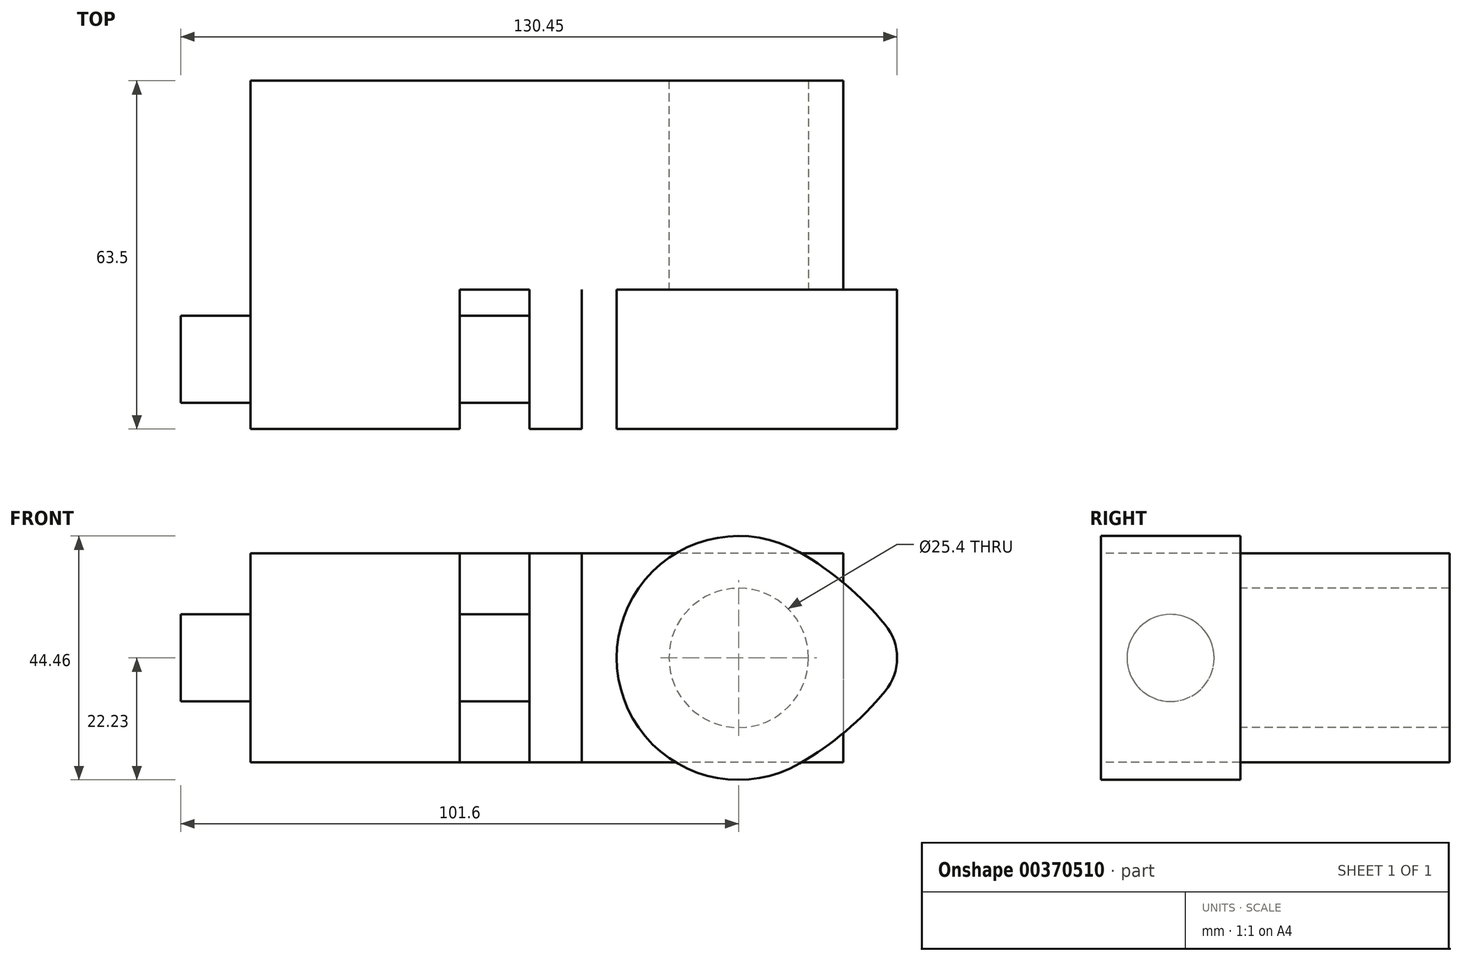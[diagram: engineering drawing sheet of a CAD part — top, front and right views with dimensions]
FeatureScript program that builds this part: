
annotation { "Feature Type Name" : "Feature", "Feature Type Description" : "" }
export const myFeature = defineFeature(function(context is Context, id is Id, definition is map)
    precondition{}
    {
        {
            var Q0;
            Q0=qCreatedBy(makeId("Front.planeOp"),FACE);
            var sketch = newSketch(context, id + "F0", { "sketchPlane" : qUnion([Q0])});
            skArc(sketch, "E0", {"start": v(11.11, 19.25) * mm, "mid": v(-22.22, 0) * mm, "end": v(11.11, -19.25) * mm});
            skLineSegment(sketch, "E1", {"start": v(0, 0) * mm, "end": v(-21.9, 37.92) * mm, "construction": true});
            skArc(sketch, "E2", {"start": v(11.11, -19.25) * mm, "mid": v(19.5, -13.35) * mm, "end": v(26.68, -6.05) * mm});
            skLineSegment(sketch, "E3", {"start": v(0, 0) * mm, "end": v(-17.46, -30.25) * mm, "construction": true});
            skArc(sketch, "E4", {"start": v(26.68, 6.05) * mm, "mid": v(19.5, 13.35) * mm, "end": v(11.11, 19.25) * mm});
            skCircle(sketch, "E5", {"center": v(0, 0) * mm, "radius": 12.7 * mm});
            skPoint(sketch, "E6.visualSharp", {"position": v(31.03, 0) * mm});
            skArc(sketch, "E6.filletArc", {"start": v(26.68, -6.05) * mm, "mid": v(28.85, 0) * mm, "end": v(26.68, 6.05) * mm});
            skSolve(sketch);
        }
        {
            var Q0;
            Q0=makeQuery(id+"F0.imprint","IMPRINT",FACE,{"disambiguationData":[TD([[makeQuery(id+"F0.imprint","IMPRINT",EDGE,{"derivedFrom":sQuery(id+"F0.wireOp",EDGE,"E0")}),1.0]])]});
            extrude(context, id + "F1", {"entities" : qUnion([Q0]), "depth" : 25.4 * mm});
        }
        {
            var Q0;
            Q0=qCreatedBy(makeId("Front.planeOp"),FACE);
            var sketch = newSketch(context, id + "F2", { "sketchPlane" : qUnion([Q0])});
            skCircle(sketch, "E7", {"center": v(0, 0) * mm, "radius": 12.7 * mm});
            skSolve(sketch);
        }
        {
            var Q0;
            Q0=qSketchRegion(id+"F2",true);
            extrude(context, id + "F3", {"entities" : qUnion([Q0]), "operationType" : NewBodyOperationType.ADD, "depth" : 25.4 * mm, "hasSecondDirection" : true, "secondDirectionOppositeDirection" : true, "secondDirectionDepth" : 38.1 * mm});
        }
        {
            var Q0;
            Q0=qCreatedBy(makeId("Front.planeOp"),FACE);
            var sketch = newSketch(context, id + "F4", { "sketchPlane" : qUnion([Q0])});
            skLineSegment(sketch, "E8.bottom", {"start": v(19.05, 19.05) * mm, "end": v(-88.9, 19.05) * mm});
            skLineSegment(sketch, "E8.top", {"start": v(19.05, -19.05) * mm, "end": v(-88.9, -19.05) * mm});
            skLineSegment(sketch, "E8.left", {"start": v(19.05, 19.05) * mm, "end": v(19.05, -19.05) * mm});
            skLineSegment(sketch, "E8.right", {"start": v(-88.9, 19.05) * mm, "end": v(-88.9, -19.05) * mm});
            skCircle(sketch, "E9", {"center": v(0, 0) * mm, "radius": 12.7 * mm});
            skLineSegment(sketch, "E10", {"start": v(0, 0) * mm, "end": v(-94.9, 0) * mm, "construction": true});
            skSolve(sketch);
        }
        {
            var Q0;
            Q0=makeQuery(id+"F4.imprint","IMPRINT",FACE,{"disambiguationData":[TD([[makeQuery(id+"F4.imprint","IMPRINT",EDGE,{"derivedFrom":sQuery(id+"F4.wireOp",EDGE,"E8.bottom")}),1.0]])]});
            extrude(context, id + "F5", {"entities" : qUnion([Q0]), "oppositeDirection" : true, "depth" : 38.1 * mm});
        }
        {
            var Q0;
            Q0=qCreatedBy(makeId("Right.planeOp"),FACE);
            var sketch = newSketch(context, id + "F6", { "sketchPlane" : qUnion([Q0])});
            skLineSegment(sketch, "E11.bottom", {"start": v(0, -19.05) * mm, "end": v(-25.4, -19.05) * mm});
            skLineSegment(sketch, "E11.top", {"start": v(0, 19.05) * mm, "end": v(-25.4, 19.05) * mm});
            skLineSegment(sketch, "E11.left", {"start": v(0, -19.05) * mm, "end": v(0, 19.05) * mm});
            skLineSegment(sketch, "E11.right", {"start": v(-25.4, -19.05) * mm, "end": v(-25.4, 19.05) * mm});
            skLineSegment(sketch, "E12", {"start": v(0, 0) * mm, "end": v(-58, 0) * mm, "construction": true});
            skCircle(sketch, "E13", {"center": v(-12.7, 0) * mm, "radius": 7.94 * mm});
            skSolve(sketch);
        }
        {
            var Q0;
            Q0=makeQuery(id+"F6.imprint","IMPRINT",FACE,{"disambiguationData":[TD([[makeQuery(id+"F6.imprint","IMPRINT",EDGE,{"derivedFrom":sQuery(id+"F6.wireOp",EDGE,"E11.bottom")}),-1.0]])]});
            extrude(context, id + "F7", {"entities" : qUnion([Q0]), "operationType" : NewBodyOperationType.ADD, "oppositeDirection" : true, "depth" : 88.9 * mm, "hasSecondDirection" : true, "secondDirectionOppositeDirection" : true, "secondDirectionDepth" : 50.8 * mm});
        }
        {
            var Q0;
            Q0=makeQuery(id+"F6.imprint","IMPRINT",FACE,{"disambiguationData":[TD([[makeQuery(id+"F6.imprint","IMPRINT",EDGE,{"derivedFrom":sQuery(id+"F6.wireOp",EDGE,"E11.bottom")}),-1.0]])]});
            extrude(context, id + "F8", {"entities" : qUnion([Q0]), "oppositeDirection" : true, "depth" : 38.1 * mm, "hasSecondDirection" : true, "secondDirectionOppositeDirection" : true, "secondDirectionDepth" : 28.57 * mm});
        }
        {
            var Q0;
            Q0=qCreatedBy(makeId("Right.planeOp"),FACE);
            var sketch = newSketch(context, id + "F9", { "sketchPlane" : qUnion([Q0])});
            skCircle(sketch, "E14", {"center": v(-12.7, 0) * mm, "radius": 7.94 * mm});
            skSolve(sketch);
        }
        {
            var Q0;
            Q0=makeQuery(id+"F9.imprint","IMPRINT",FACE,{"disambiguationData":[TD([[makeQuery(id+"F9.imprint","IMPRINT",EDGE,{"derivedFrom":sQuery(id+"F9.wireOp",EDGE,"E14")}),1.0]])]});
            var Q1;
            Q1=sQuery(id+"F9.wireOp",EDGE,"E14");
            extrude(context, id + "F10", {"entities" : qUnion([Q0]), "operationType" : NewBodyOperationType.ADD, "surfaceEntities" : qUnion([Q1]), "oppositeDirection" : true, "depth" : 101.6 * mm, "hasSecondDirection" : true, "secondDirectionOppositeDirection" : true, "secondDirectionDepth" : 28.57 * mm});
        }
    });
